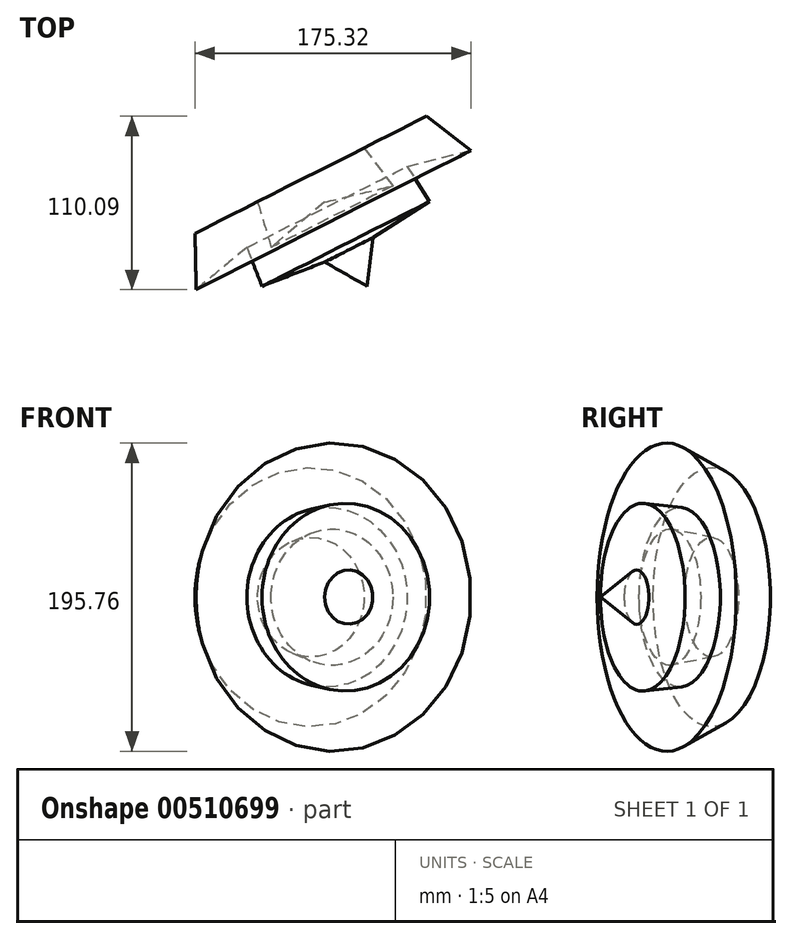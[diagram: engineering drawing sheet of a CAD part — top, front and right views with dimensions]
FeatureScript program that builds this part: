
annotation { "Feature Type Name" : "Feature", "Feature Type Description" : "" }
export const myFeature = defineFeature(function(context is Context, id is Id, definition is map)
    precondition{}
    {
        {
            var Q0;
            Q0=qCreatedBy(makeId("Top.planeOp"),FACE);
            var sketch = newSketch(context, id + "F0", { "sketchPlane" : qUnion([Q0])});
            skLineSegment(sketch, "E0", {"start": v(-57.85, -17.47) * mm, "end": v(-58.54, 18.19) * mm});
            skLineSegment(sketch, "E1", {"start": v(-58.54, 18.19) * mm, "end": v(-18.77, 38.07) * mm});
            skLineSegment(sketch, "E2", {"start": v(-18.77, 38.07) * mm, "end": v(-10.2, 9.27) * mm});
            skLineSegment(sketch, "E3", {"start": v(-10.2, 9.27) * mm, "end": v(23.73, 38.07) * mm});
            skLineSegment(sketch, "E4", {"start": v(23.73, 38.07) * mm, "end": v(50.82, -15.4) * mm});
            skLineSegment(sketch, "E5", {"start": v(50.82, -15.4) * mm, "end": v(23.73, 0) * mm});
            skLineSegment(sketch, "E6", {"start": v(23.73, 0) * mm, "end": v(-16.03, -15.4) * mm});
            skLineSegment(sketch, "E7", {"start": v(-16.03, -15.4) * mm, "end": v(-25.6, 9.27) * mm});
            skLineSegment(sketch, "E8", {"start": v(-25.6, 9.27) * mm, "end": v(-57.85, -17.47) * mm});
            skSolve(sketch);
        }
        {
            var Q0;
            Q0=makeQuery(id+"F0.imprint","IMPRINT",FACE,{"disambiguationData":[TD([[makeQuery(id+"F0.imprint","IMPRINT",EDGE,{"derivedFrom":sQuery(id+"F0.wireOp",EDGE,"E0")}),-1.0]])]});
            var Q1;
            Q1=sQuery(id+"F0.wireOp",EDGE,"E4");
            revolve(context, id + "F1", {"entities" : qUnion([Q0]), "axis" : qUnion([Q1]), "revolveType" : RevolveType.FULL});
        }
    });
